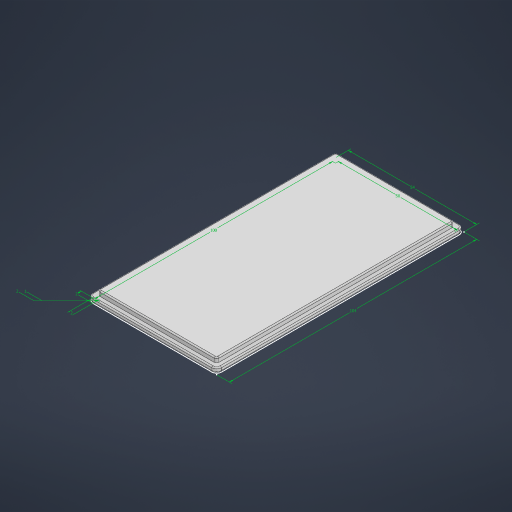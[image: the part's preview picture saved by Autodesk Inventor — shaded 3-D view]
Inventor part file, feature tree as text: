
AUTODESK INVENTOR PART (.ipt)
format: ipt  version: 2024.2 (Build 282272000, 272)  size: 235,520 bytes
history: native  units: mm
features: extrude x2, sketch x1, fillet x1
ambient origin geometry x8: Origin, YZ Plane, XZ Plane, XY Plane, X Axis, Y Axis, Z Axis, Center Point
bodies: Solid1 (feature_tree)
feature tree (4):
  sketch  "Sketch1"  dims[d0=50.0mm d1=100.0mm d2=54.0mm d3=104.0mm d4=2.0mm d5=2.0mm d6=2.0mm d7=1.0mm d8=4.0mm d9=0.0mm d10=2.0mm d11=0.0mm d12=0.5mm]
  extrude  "Extrusion1"  Depth=100.0mm
  extrude  "Extrusion2"  Depth=54.0mm
  fillet  "Fillet1"  Radius=104.0mm
